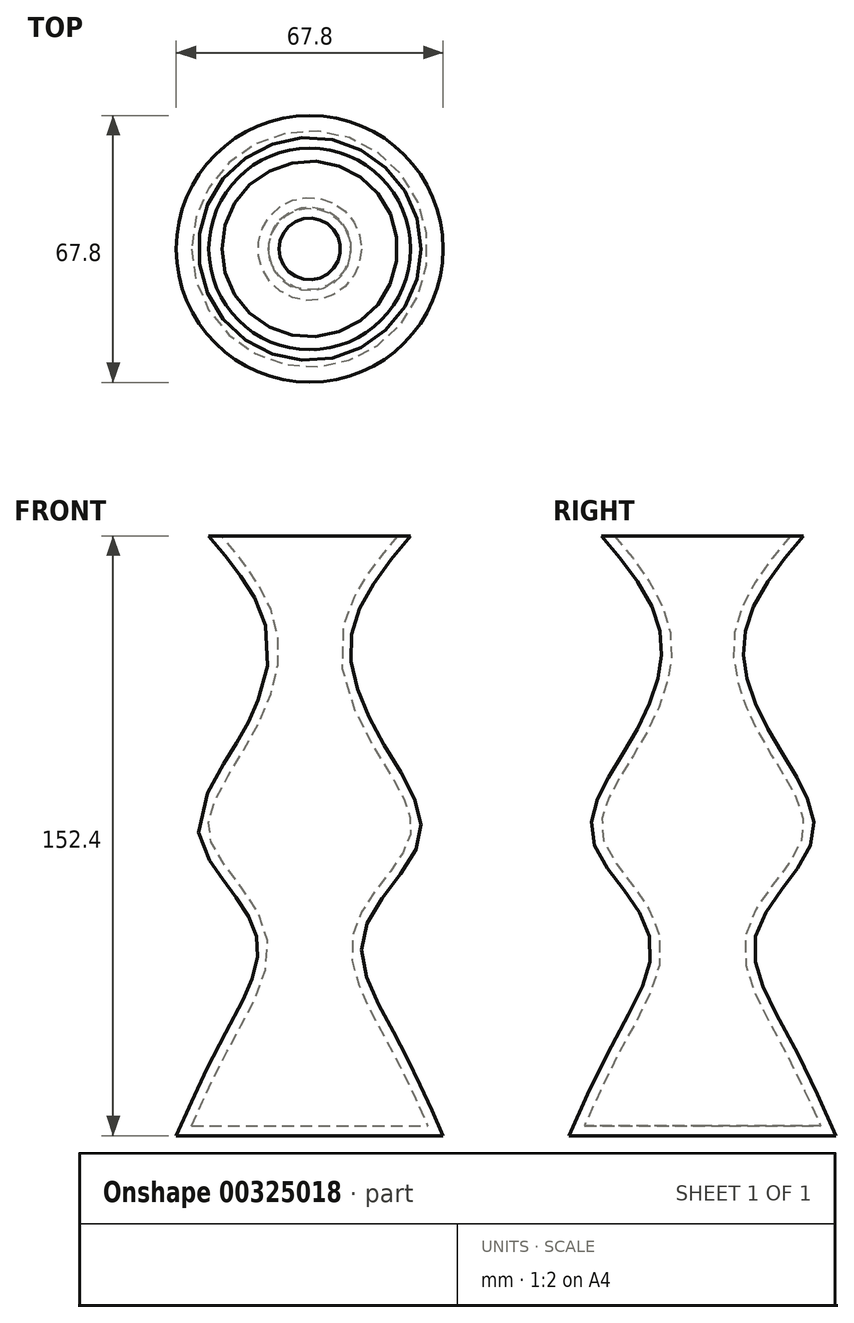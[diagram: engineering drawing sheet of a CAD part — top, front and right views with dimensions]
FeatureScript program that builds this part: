
annotation { "Feature Type Name" : "Feature", "Feature Type Description" : "" }
export const myFeature = defineFeature(function(context is Context, id is Id, definition is map)
    precondition{}
    {
        {
            var Q0;
            Q0=qCreatedBy(makeId("Top.planeOp"),FACE);
            cPlane(context, id + "F0", {"entities" : qUnion([Q0]), "cplaneType" : CPlaneType.OFFSET, "offset" : 25.4 * mm, "width" : 152.4 * mm, "height" : 152.4 * mm});
        }
        {
            var Q0;
            Q0=qCreatedBy(id+"F0.planeOp",FACE);
            cPlane(context, id + "F1", {"entities" : qUnion([Q0]), "cplaneType" : CPlaneType.OFFSET, "offset" : 25.4 * mm, "width" : 152.4 * mm, "height" : 152.4 * mm});
        }
        {
            var Q0;
            Q0=qCreatedBy(id+"F1.planeOp",FACE);
            cPlane(context, id + "F2", {"entities" : qUnion([Q0]), "cplaneType" : CPlaneType.OFFSET, "offset" : 25.4 * mm, "width" : 152.4 * mm, "height" : 152.4 * mm});
        }
        {
            var Q0;
            Q0=qCreatedBy(id+"F2.planeOp",FACE);
            cPlane(context, id + "F3", {"entities" : qUnion([Q0]), "cplaneType" : CPlaneType.OFFSET, "offset" : 25.4 * mm, "width" : 152.4 * mm, "height" : 152.4 * mm});
        }
        {
            var Q0;
            Q0=qCreatedBy(makeId("Top.planeOp"),FACE);
            cPlane(context, id + "F4", {"entities" : qUnion([Q0]), "cplaneType" : CPlaneType.OFFSET, "offset" : 25.4 * mm, "oppositeDirection" : true, "width" : 152.4 * mm, "height" : 152.4 * mm});
        }
        {
            var Q0;
            Q0=qCreatedBy(id+"F4.planeOp",FACE);
            cPlane(context, id + "F5", {"entities" : qUnion([Q0]), "cplaneType" : CPlaneType.OFFSET, "offset" : 25.4 * mm, "oppositeDirection" : true, "width" : 152.4 * mm, "height" : 152.4 * mm});
        }
        {
            var Q0;
            Q0=qCreatedBy(id+"F5.planeOp",FACE);
            var sketch = newSketch(context, id + "F6", { "sketchPlane" : qUnion([Q0])});
            skCircle(sketch, "E0", {"center": v(0, 0) * mm, "radius": 33.9 * mm});
            skSolve(sketch);
        }
        {
            var Q0;
            Q0=qCreatedBy(id+"F4.planeOp",FACE);
            var sketch = newSketch(context, id + "F7", { "sketchPlane" : qUnion([Q0])});
            skCircle(sketch, "E1", {"center": v(0, 0) * mm, "radius": 21.75 * mm});
            skSolve(sketch);
        }
        {
            var Q0;
            Q0=qCreatedBy(id+"F3.planeOp",FACE);
            var sketch = newSketch(context, id + "F8", { "sketchPlane" : qUnion([Q0])});
            skCircle(sketch, "E2", {"center": v(0, 0) * mm, "radius": 25.63 * mm});
            skSolve(sketch);
        }
        {
            var Q0;
            Q0=qCreatedBy(id+"F2.planeOp",FACE);
            var sketch = newSketch(context, id + "F9", { "sketchPlane" : qUnion([Q0])});
            skCircle(sketch, "E3", {"center": v(0, 0) * mm, "radius": 10.61 * mm});
            skSolve(sketch);
        }
        {
            var Q0;
            Q0=qCreatedBy(id+"F1.planeOp",FACE);
            var sketch = newSketch(context, id + "F10", { "sketchPlane" : qUnion([Q0])});
            skCircle(sketch, "E4", {"center": v(0, 0) * mm, "radius": 17.53 * mm});
            skSolve(sketch);
        }
        {
            var Q0;
            Q0=qCreatedBy(id+"F0.planeOp",FACE);
            var sketch = newSketch(context, id + "F11", { "sketchPlane" : qUnion([Q0])});
            skCircle(sketch, "E5", {"center": v(0, 0) * mm, "radius": 28.1 * mm});
            skSolve(sketch);
        }
        {
            var Q0;
            Q0=qCreatedBy(makeId("Top.planeOp"),FACE);
            var sketch = newSketch(context, id + "F12", { "sketchPlane" : qUnion([Q0])});
            skCircle(sketch, "E6", {"center": v(0, 0) * mm, "radius": 13.48 * mm});
            skSolve(sketch);
        }
        {
            var Q0;
            Q0=makeQuery(id+"F6.imprint","IMPRINT",FACE,{"disambiguationData":[TD([[makeQuery(id+"F6.imprint","IMPRINT",EDGE,{"derivedFrom":sQuery(id+"F6.wireOp",EDGE,"E0")}),1.0]])]});
            var Q1;
            Q1=makeQuery(id+"F7.imprint","IMPRINT",FACE,{"disambiguationData":[TD([[makeQuery(id+"F7.imprint","IMPRINT",EDGE,{"derivedFrom":sQuery(id+"F7.wireOp",EDGE,"E1")}),1.0]])]});
            var Q2;
            Q2=makeQuery(id+"F12.imprint","IMPRINT",FACE,{"disambiguationData":[TD([[makeQuery(id+"F12.imprint","IMPRINT",EDGE,{"derivedFrom":sQuery(id+"F12.wireOp",EDGE,"E6")}),1.0]])]});
            var Q3;
            Q3=makeQuery(id+"F11.imprint","IMPRINT",FACE,{"disambiguationData":[TD([[makeQuery(id+"F11.imprint","IMPRINT",EDGE,{"derivedFrom":sQuery(id+"F11.wireOp",EDGE,"E5")}),1.0]])]});
            var Q4;
            Q4=makeQuery(id+"F10.imprint","IMPRINT",FACE,{"disambiguationData":[TD([[makeQuery(id+"F10.imprint","IMPRINT",EDGE,{"derivedFrom":sQuery(id+"F10.wireOp",EDGE,"E4")}),1.0]])]});
            var Q5;
            Q5=makeQuery(id+"F9.imprint","IMPRINT",FACE,{"disambiguationData":[TD([[makeQuery(id+"F9.imprint","IMPRINT",EDGE,{"derivedFrom":sQuery(id+"F9.wireOp",EDGE,"E3")}),1.0]])]});
            var Q6;
            Q6=makeQuery(id+"F8.imprint","IMPRINT",FACE,{"disambiguationData":[TD([[makeQuery(id+"F8.imprint","IMPRINT",EDGE,{"derivedFrom":sQuery(id+"F8.wireOp",EDGE,"E2")}),1.0]])]});
            loft(context, id + "F13", {"sheetProfilesArray" : [{ "sheetProfileEntities" : qUnion([Q0]) }, { "sheetProfileEntities" : qUnion([Q1]) }, { "sheetProfileEntities" : qUnion([Q2]) }, { "sheetProfileEntities" : qUnion([Q3]) }, { "sheetProfileEntities" : qUnion([Q4]) }, { "sheetProfileEntities" : qUnion([Q5]) }, { "sheetProfileEntities" : qUnion([Q6]) }]});
        }
        {
            var Q0;
            Q0=makeQuery(id+"F13.opLoft","CAP_FACE",FACE,{"disambiguationData":[OSD([makeQuery(id+"F8.imprint","IMPRINT",FACE,{"disambiguationData":[TD([[makeQuery(id+"F8.imprint","IMPRINT",EDGE,{"derivedFrom":sQuery(id+"F8.wireOp",EDGE,"E2")}),1.0]])]})])],"isStart":true});
            shell(context, id + "F14", {"entities" : qUnion([Q0]), "thickness" : 2.54 * mm});
        }
    });
